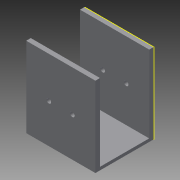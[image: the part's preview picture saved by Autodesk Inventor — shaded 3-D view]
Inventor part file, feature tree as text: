
AUTODESK INVENTOR PART (.ipt)
format: ipt  version: 2013 (Build 170138000, 138)  size: 98,304 bytes
history: native  units: mm
features: sketch x4, extrude x2, other x1, hole x1
ambient origin geometry x8: Origin, YZ Plane, XZ Plane, XY Plane, X Axis, Y Axis, Z Axis, Center Point
feature tree (8):
  other  "ソリッド1"
  extrude  "押し出し1"  Depth=45.0mm
  extrude  "押し出し2"  Depth=2.0mm
  sketch  "スケッチ3"
  hole  "穴1"  [1 undecoded]
  sketch  "スケッチ1"
  sketch  "スケッチ2"
  sketch  "スケッチ4"
note: 1 required parameter value undecoded (feature->parameter linkage not recoverable at this tier; creation-order binding heuristic only, values carry confidence <= 0.55)
